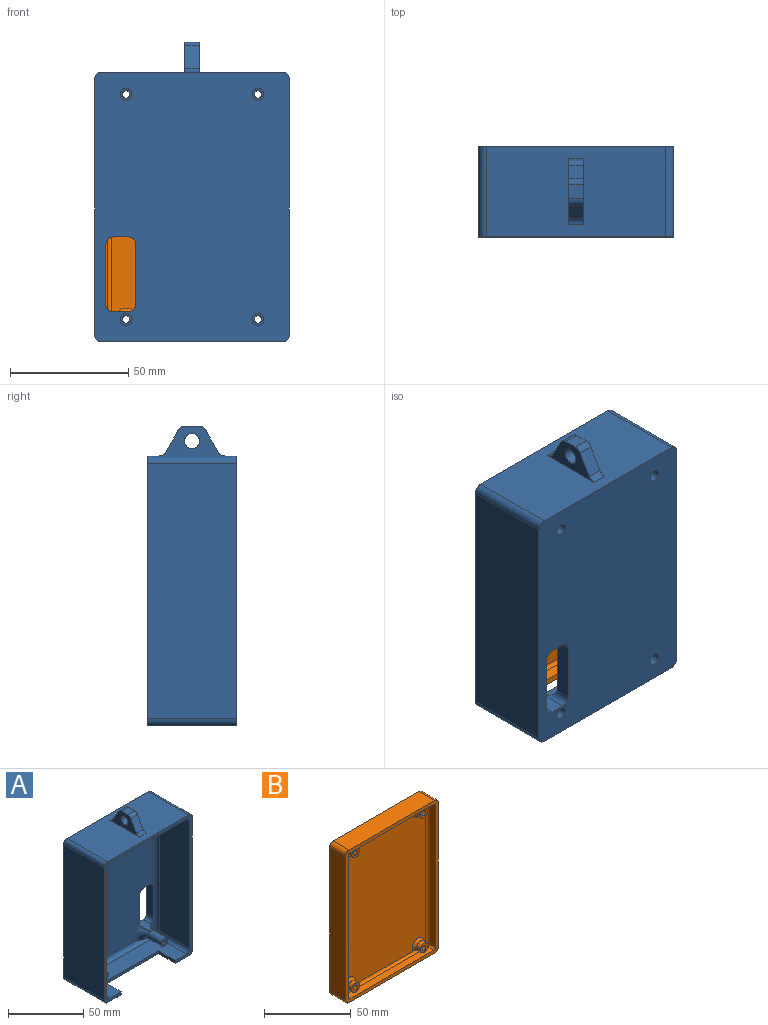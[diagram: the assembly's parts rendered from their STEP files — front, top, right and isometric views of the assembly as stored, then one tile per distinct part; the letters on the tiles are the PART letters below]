
ASSEMBLY  parts=2 mates=1
PART A: 72 faces, bbox 86.4x38.2x132.8 mm
  f0: plane 114.3x82.55mm, normal (0,1,0), area 8951.2mm2, adj f8,f9,f10,f11,f35,f36,f37,f38
  f1: plane 103.19x71.44mm, normal (0,-1,0), area 6247.2mm2, adj f2,f27,f28,f32,f39,f40,f41,f42
  f2: cylinder r=3.17mm len=103.19mm, axis (0,0,1), area 482.5mm2, adj f1,f12,f30,f33,f39,f40,f54,f58
  f3: cylinder r=1.59mm len=20.64mm, axis (0,-1,0), area 205.8mm2, adj f23,f53
  f4: cylinder r=1.59mm len=20.64mm, axis (0,-1,0), area 205.8mm2, adj f21,f51
  f5: cylinder r=1.59mm len=20.64mm, axis (0,-1,0), area 205.8mm2, adj f19,f49
  f6: cylinder r=1.59mm len=20.64mm, axis (0,-1,0), area 205.8mm2, adj f17,f47
  f7: plane 114.3x82.55mm, normal (0,-1,0), area 793.8mm2, adj f8,f9,f10,f11,f12,f13,f14,f15
  f8: plane 107.95x38.1mm, normal (1,0,0), area 4112.9mm2, adj f0,f7,f35,f38
  f9: plane 76.2x38.1mm, normal (0,0,1), area 2726.3mm2, adj f0,f7,f35,f36,f66,f67,f68,f71
  f10: plane 107.95x38.1mm, normal (-1,0,0), area 4112.9mm2, adj f0,f7,f36,f37
  f11: plane 76.2x38.1mm, normal (0,0,-1), area 2096.8mm2, adj f0,f7,f37,f38,f43,f44,f45
  f12: plane 103.19x28.58mm, normal (-1,0,0), area 2948.6mm2, adj f2,f7,f26,f34
  f13: plane 71.44x28.58mm, normal (0,0,-1), area 2041.3mm2, adj f7,f29,f32,f34
  f14: plane 103.19x28.58mm, normal (1,0,0), area 2948.6mm2, adj f7,f24,f28,f29
  f15: plane 71.44x28.58mm, normal (0,0,1), area 1234.9mm2, adj f7,f24,f26,f27,f43,f44,f45
  f16: cylinder r=3.17mm len=12.7mm, axis (0,1,0), area 253.4mm2, adj f17,f42
  f17: plane 6.35x6.35mm, normal (0,-1,0), area 23.8mm2, adj f6,f16
  f18: cylinder r=3.17mm len=12.7mm, axis (0,1,0), area 253.4mm2, adj f19,f39
  f19: plane 6.35x6.35mm, normal (0,-1,0), area 23.8mm2, adj f5,f18
  f20: cylinder r=3.17mm len=12.7mm, axis (0,1,0), area 253.4mm2, adj f21,f41
  f21: plane 6.35x6.35mm, normal (0,-1,0), area 23.8mm2, adj f4,f20
  f22: cylinder r=3.17mm len=12.7mm, axis (0,1,0), area 253.4mm2, adj f23,f40
  f23: plane 6.35x6.35mm, normal (0,-1,0), area 23.8mm2, adj f3,f22
  f24: cylinder r=3.17mm len=28.58mm, axis (0,-1,0), area 142.5mm2, adj f7,f14,f15,f25
  f25: sphere r=3.17mm, area 15.8mm2, adj f24,f27,f28,f41
  f26: cylinder r=3.17mm len=28.58mm, axis (0,1,0), area 142.5mm2, adj f7,f12,f15,f30
  f27: cylinder r=3.17mm len=71.44mm, axis (1,0,0), area 301.4mm2, adj f1,f15,f25,f30,f40,f41
  f28: cylinder r=3.17mm len=103.19mm, axis (0,0,-1), area 504.6mm2, adj f1,f14,f25,f31,f41,f42
  f29: cylinder r=3.17mm len=28.58mm, axis (0,1,0), area 142.5mm2, adj f7,f13,f14,f31
  f30: sphere r=3.17mm, area 15.8mm2, adj f2,f26,f27,f40
  f31: sphere r=3.17mm, area 15.8mm2, adj f28,f29,f32,f42
  f32: cylinder r=3.17mm len=71.44mm, axis (-1,0,0), area 301.4mm2, adj f1,f13,f31,f33,f39,f42
  f33: sphere r=3.17mm, area 15.7mm2, adj f2,f32,f34,f39
  f34: cylinder r=3.17mm len=28.58mm, axis (0,-1,0), area 142.5mm2, adj f7,f12,f13,f33
  f35: cylinder r=3.17mm len=38.1mm, axis (0,-1,0), area 190mm2, adj f0,f7,f8,f9
  f36: cylinder r=3.17mm len=38.1mm, axis (0,1,0), area 190mm2, adj f0,f7,f9,f10
  f37: cylinder r=3.17mm len=38.1mm, axis (0,-1,0), area 190mm2, adj f0,f7,f10,f11
  f38: cylinder r=3.17mm len=38.1mm, axis (0,1,0), area 190mm2, adj f0,f7,f8,f11
  f39: torus R=9.53mm, axis (0,-1,0), area 291.4mm2, adj f1,f2,f18,f32,f33
  f40: torus R=9.53mm, axis (0,-1,0), area 214.8mm2, adj f1,f2,f22,f27,f30,f55,f57,f59
  f41: torus R=9.53mm, axis (0,-1,0), area 291.4mm2, adj f1,f20,f25,f27,f28
  f42: torus R=9.53mm, axis (0,-1,0), area 291.4mm2, adj f1,f16,f28,f31,f32
  f43: plane 15.88x2.38mm, normal (1,0,0), area 37.8mm2, adj f7,f11,f15,f44
  f44: plane 50.8x2.38mm, normal (0,-1,0), area 121mm2, adj f11,f15,f43,f45
  f45: plane 15.88x2.38mm, normal (-1,0,0), area 37.8mm2, adj f7,f11,f15,f44
  f46: cylinder r=2.54mm len=5.08mm, axis (0,1,0), area 76mm2, adj f0,f47
  f47: plane 5.08x5.08mm, normal (0,1,0), area 12.4mm2, adj f6,f46
  f48: cylinder r=2.54mm len=5.08mm, axis (0,1,0), area 76mm2, adj f0,f49
  f49: plane 5.08x5.08mm, normal (0,1,0), area 12.4mm2, adj f5,f48
  f50: cylinder r=2.54mm len=5.08mm, axis (0,1,0), area 76mm2, adj f0,f51
  f51: plane 5.08x5.08mm, normal (0,1,0), area 12.4mm2, adj f4,f50
  f52: cylinder r=2.54mm len=5.08mm, axis (0,1,0), area 76mm2, adj f0,f53
  f53: plane 5.08x5.08mm, normal (0,1,0), area 12.4mm2, adj f3,f52
  f54: plane 25.4x6.45mm, normal (-1,0,0), area 163.9mm2, adj f0,f2,f58,f59
  f55: plane 12.71x6.37mm, normal (0,0,1), area 62.9mm2, adj f0,f40,f59,f60
  f56: plane 6.35x6.35mm, normal (0,0,-1), area 40.3mm2, adj f0,f1,f58,f61
  f57: plane 25.52x6.78mm, normal (1,0,0), area 161.5mm2, adj f0,f1,f40,f60,f61
  f58: cylinder r=3.17mm len=6.45mm, axis (0,1,0), area 31.8mm2, adj f0,f1,f2,f54,f56
  f59: cylinder r=3.17mm len=7.25mm, axis (0,-1,0), area 33.2mm2, adj f0,f2,f40,f54,f55
  f60: cylinder r=3.17mm len=11.38mm, axis (0,1,0), area 41.9mm2, adj f0,f40,f55,f57
  f61: cylinder r=3.17mm len=6.35mm, axis (0,-1,0), area 31.7mm2, adj f0,f1,f56,f57
  f62: plane 9.53x6.35mm, normal (0,0.87,0.5), area 69.8mm2, adj f66,f67,f68,f69
  f63: plane 6.35x5.86mm, normal (0,0,1), area 37.2mm2, adj f66,f67,f69,f70
  f64: plane 9.53x6.35mm, normal (0,-0.87,0.5), area 69.8mm2, adj f66,f67,f70,f71
  f65: cylinder r=3.17mm len=6.35mm, axis (-1,0,0), area 126.7mm2, adj f66,f67
  f66: plane 27.86x12.7mm, normal (1,0,0), area 182.4mm2, adj f9,f62,f63,f64,f65,f68,f69,f70
  f67: plane 27.86x12.7mm, normal (-1,0,0), area 182.4mm2, adj f9,f62,f63,f64,f65,f68,f69,f70
  f68: cylinder r=3.17mm len=6.35mm, axis (-1,0,0), area 21.1mm2, adj f9,f62,f66,f67
  f69: cylinder r=3.17mm len=6.35mm, axis (-1,0,0), area 21.1mm2, adj f62,f63,f66,f67
  f70: cylinder r=3.17mm len=6.35mm, axis (1,0,0), area 21.1mm2, adj f63,f64,f66,f67
  f71: cylinder r=3.17mm len=6.35mm, axis (1,0,0), area 21.1mm2, adj f9,f64,f66,f67
PART B: 71 faces, bbox 76.2x12.7x108 mm
  f0: cylinder r=1.59mm len=7.94mm, axis (0,-1,0), area 79.2mm2, adj f22,f70
  f1: cylinder r=1.59mm len=7.94mm, axis (0,-1,0), area 79.2mm2, adj f20,f63
  f2: cylinder r=1.59mm len=7.94mm, axis (0,-1,0), area 79.2mm2, adj f18,f56
  f3: cylinder r=1.59mm len=7.94mm, axis (0,-1,0), area 79.2mm2, adj f16,f49
  f4: plane 107.95x76.2mm, normal (0,-1,0), area 847.8mm2, adj f5,f6,f7,f8,f10,f11,f12,f13
  f5: plane 101.6x12.7mm, normal (1,0,0), area 1290.3mm2, adj f4,f9,f39,f42
  f6: plane 69.85x12.7mm, normal (0,0,1), area 887.1mm2, adj f4,f9,f39,f40
  f7: plane 101.6x12.7mm, normal (-1,0,0), area 1290.3mm2, adj f4,f9,f40,f41
  f8: plane 69.85x12.7mm, normal (0,0,-1), area 887.1mm2, adj f4,f9,f41,f42
  f9: plane 107.95x76.2mm, normal (0,1,0), area 8048.1mm2, adj f5,f6,f7,f8,f39,f40,f41,f42
  f10: plane 100.01x4.76mm, normal (-1,0,0), area 476.3mm2, adj f4,f25,f32,f33
  f11: plane 68.26x4.76mm, normal (0,0,-1), area 325.1mm2, adj f4,f31,f32,f37
  f12: plane 100.01x4.76mm, normal (1,0,0), area 476.3mm2, adj f4,f24,f30,f31
  f13: plane 68.26x4.76mm, normal (0,0,1), area 325.1mm2, adj f4,f24,f25,f27
  f14: plane 100.01x68.26mm, normal (0,-1,0), area 6597.8mm2, adj f23,f26,f27,f30,f33,f34,f37,f38
  f15: cylinder r=3.17mm len=6.35mm, axis (0,1,0), area 63.3mm2, adj f16,f34
  f16: plane 6.35x6.35mm, normal (0,-1,0), area 23.8mm2, adj f3,f15
  f17: cylinder r=3.17mm len=6.35mm, axis (0,1,0), area 63.3mm2, adj f18,f38
  f18: plane 6.35x6.35mm, normal (0,-1,0), area 23.8mm2, adj f2,f17
  f19: cylinder r=3.17mm len=6.35mm, axis (0,1,0), area 63.3mm2, adj f20,f23
  f20: plane 6.35x6.35mm, normal (0,-1,0), area 23.8mm2, adj f1,f19
  f21: cylinder r=3.17mm len=6.35mm, axis (0,1,0), area 63.3mm2, adj f22,f26
  f22: plane 6.35x6.35mm, normal (0,-1,0), area 23.8mm2, adj f0,f21
  f23: torus R=4.76mm, axis (0,-1,0), area 50.8mm2, adj f14,f19,f27
  f24: cylinder r=1.59mm len=4.76mm, axis (0,-1,0), area 11.9mm2, adj f4,f12,f13,f28
  f25: cylinder r=1.59mm len=4.76mm, axis (0,1,0), area 11.9mm2, adj f4,f10,f13,f29
  f26: torus R=4.76mm, axis (0,-1,0), area 50.8mm2, adj f14,f21,f27
  f27: cylinder r=1.59mm len=68.26mm, axis (1,0,0), area 156mm2, adj f13,f14,f23,f26,f28,f29
  f28: sphere r=1.59mm, area 4mm2, adj f24,f27,f30
  f29: sphere r=1.59mm, area 4mm2, adj f25,f27,f33
  f30: cylinder r=1.59mm len=100.01mm, axis (0,0,-1), area 249.4mm2, adj f12,f14,f28,f35
  f31: cylinder r=1.59mm len=4.76mm, axis (0,1,0), area 11.9mm2, adj f4,f11,f12,f35
  f32: cylinder r=1.59mm len=4.76mm, axis (0,-1,0), area 11.9mm2, adj f4,f10,f11,f36
  f33: cylinder r=1.59mm len=100.01mm, axis (0,0,1), area 249.4mm2, adj f10,f14,f29,f36
  f34: torus R=4.76mm, axis (0,-1,0), area 50.8mm2, adj f14,f15,f37
  f35: sphere r=1.59mm, area 4mm2, adj f30,f31,f37
  f36: sphere r=1.59mm, area 4mm2, adj f32,f33,f37
  f37: cylinder r=1.59mm len=68.26mm, axis (-1,0,0), area 156mm2, adj f11,f14,f34,f35,f36,f38
  f38: torus R=4.76mm, axis (0,-1,0), area 50.8mm2, adj f14,f17,f37
  f39: cylinder r=3.17mm len=12.7mm, axis (0,-1,0), area 63.3mm2, adj f4,f5,f6,f9
  f40: cylinder r=3.17mm len=12.7mm, axis (0,1,0), area 63.3mm2, adj f4,f6,f7,f9
  f41: cylinder r=3.17mm len=12.7mm, axis (0,-1,0), area 63.3mm2, adj f4,f7,f8,f9
  f42: cylinder r=3.17mm len=12.7mm, axis (0,1,0), area 63.3mm2, adj f4,f5,f8,f9
  f43: plane 4.03x3.18mm, normal (0,0,1), area 12.8mm2, adj f9,f44,f48,f49
  f44: plane 3.49x3.18mm, normal (0.87,0,0.5), area 12.8mm2, adj f9,f43,f45,f49
  f45: plane 3.49x3.18mm, normal (0.87,0,-0.5), area 12.8mm2, adj f9,f44,f46,f49
  f46: plane 4.03x3.18mm, normal (0,0,-1), area 12.8mm2, adj f9,f45,f47,f49
  f47: plane 3.49x3.18mm, normal (-0.87,0,-0.5), area 12.8mm2, adj f9,f46,f48,f49
  f48: plane 3.49x3.18mm, normal (-0.87,0,0.5), area 12.8mm2, adj f9,f43,f47,f49
  f49: plane 8.07x6.99mm, normal (0,1,0), area 34.3mm2, adj f3,f43,f44,f45,f46,f47,f48
  f50: plane 4.03x3.18mm, normal (0,0,1), area 12.8mm2, adj f9,f51,f55,f56
  f51: plane 3.49x3.18mm, normal (0.87,0,0.5), area 12.8mm2, adj f9,f50,f52,f56
  f52: plane 3.49x3.18mm, normal (0.87,0,-0.5), area 12.8mm2, adj f9,f51,f53,f56
  f53: plane 4.03x3.18mm, normal (0,0,-1), area 12.8mm2, adj f9,f52,f54,f56
  f54: plane 3.49x3.18mm, normal (-0.87,0,-0.5), area 12.8mm2, adj f9,f53,f55,f56
  f55: plane 3.49x3.18mm, normal (-0.87,0,0.5), area 12.8mm2, adj f9,f50,f54,f56
  f56: plane 8.07x6.99mm, normal (0,1,0), area 34.3mm2, adj f2,f50,f51,f52,f53,f54,f55
  f57: plane 3.49x3.18mm, normal (0.87,0,-0.5), area 12.8mm2, adj f9,f58,f62,f63
  f58: plane 4.03x3.18mm, normal (0,0,-1), area 12.8mm2, adj f9,f57,f59,f63
  f59: plane 3.49x3.18mm, normal (-0.87,0,-0.5), area 12.8mm2, adj f9,f58,f60,f63
  f60: plane 3.49x3.18mm, normal (-0.87,0,0.5), area 12.8mm2, adj f9,f59,f61,f63
  f61: plane 4.03x3.18mm, normal (0,0,1), area 12.8mm2, adj f9,f60,f62,f63
  f62: plane 3.49x3.18mm, normal (0.87,0,0.5), area 12.8mm2, adj f9,f57,f61,f63
  f63: plane 8.07x6.99mm, normal (0,1,0), area 34.3mm2, adj f1,f57,f58,f59,f60,f61,f62
  f64: plane 3.49x3.18mm, normal (0.87,0,-0.5), area 12.8mm2, adj f9,f65,f69,f70
  f65: plane 4.03x3.18mm, normal (0,0,-1), area 12.8mm2, adj f9,f64,f66,f70
  f66: plane 3.49x3.18mm, normal (-0.87,0,-0.5), area 12.8mm2, adj f9,f65,f67,f70
  f67: plane 3.49x3.18mm, normal (-0.87,0,0.5), area 12.8mm2, adj f9,f66,f68,f70
  f68: plane 4.03x3.18mm, normal (0,0,1), area 12.8mm2, adj f9,f67,f69,f70
  f69: plane 3.49x3.18mm, normal (0.87,0,0.5), area 12.8mm2, adj f9,f64,f68,f70
  f70: plane 8.07x6.99mm, normal (0,1,0), area 34.3mm2, adj f0,f64,f65,f66,f67,f68,f69
PLACE A rot(axis=(0,0,1),180deg) t=(122.33,-11.33,-13.52)mm
PLACE B t=(122.33,26.77,-13.52)mm
MATE fastened A.f6 <-> B.f2  axis (0,1,0) through (150.27,14.07,34.1)mm
